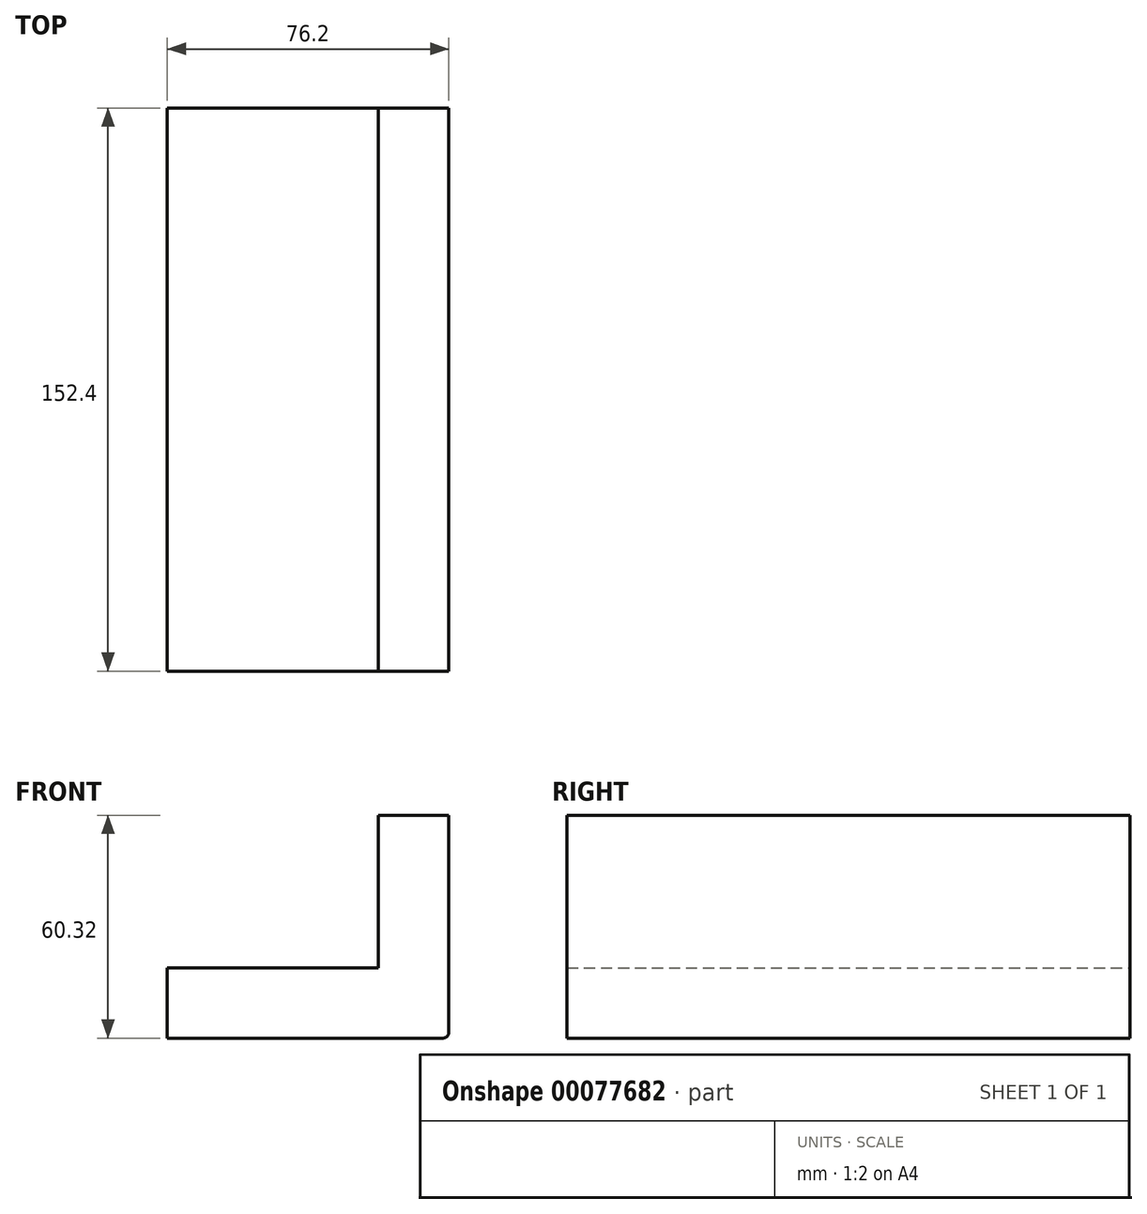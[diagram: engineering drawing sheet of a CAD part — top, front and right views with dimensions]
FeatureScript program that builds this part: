
annotation { "Feature Type Name" : "Feature", "Feature Type Description" : "" }
export const myFeature = defineFeature(function(context is Context, id is Id, definition is map)
    precondition{}
    {
        {
            var Q0;
            Q0=qCreatedBy(makeId("Front.planeOp"),FACE);
            var sketch = newSketch(context, id + "F0", { "sketchPlane" : qUnion([Q0])});
            skLineSegment(sketch, "E0", {"start": v(19.05, 30.16) * mm, "end": v(19.05, -30.16) * mm});
            skLineSegment(sketch, "E1", {"start": v(38.1, -28.58) * mm, "end": v(38.1, 30.16) * mm});
            skLineSegment(sketch, "E2", {"start": v(19.05, -30.16) * mm, "end": v(36.51, -30.16) * mm});
            skLineSegment(sketch, "E3", {"start": v(19.05, -30.16) * mm, "end": v(-38.1, -30.16) * mm});
            skLineSegment(sketch, "E4", {"start": v(-38.1, -30.16) * mm, "end": v(-38.1, -11.11) * mm});
            skLineSegment(sketch, "E5", {"start": v(-38.1, -11.11) * mm, "end": v(19.05, -11.11) * mm});
            skLineSegment(sketch, "E6", {"start": v(19.05, 30.16) * mm, "end": v(38.1, 30.16) * mm});
            skArc(sketch, "E7", {"start": v(36.51, -30.16) * mm, "mid": v(37.64, -29.7) * mm, "end": v(38.1, -28.58) * mm});
            skSolve(sketch);
        }
        {
            var Q0;
            {var subQ0=sQuery(id+"F0.wireOp",EDGE,"E3");Q0=makeQuery(id+"F0.imprint","IMPRINT",FACE,{"disambiguationData":[TD([[makeQuery(id+"F0.imprint","IMPRINT",EDGE,{"derivedFrom":subQ0}),-1.0]])]});}
            var Q1;
            Q1=makeQuery(id+"F0.imprint","IMPRINT",FACE,{"disambiguationData":[TD([[makeQuery(id+"F0.imprint","IMPRINT",EDGE,{"derivedFrom":sQuery(id+"F0.wireOp",EDGE,"E1")}),1.0]])]});
            extrude(context, id + "F1", {"entities" : qUnion([Q0, Q1]), "depth" : 152.4 * mm});
        }
    });
